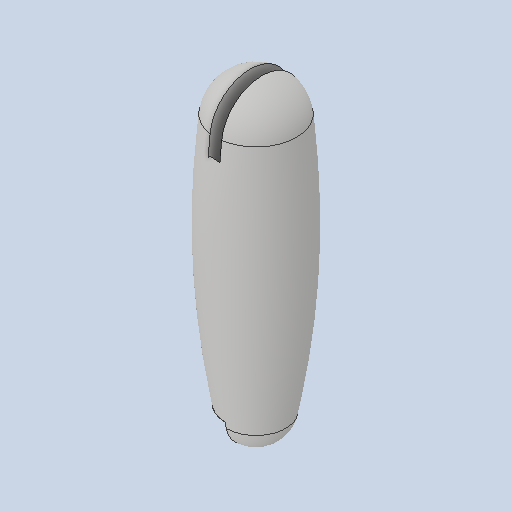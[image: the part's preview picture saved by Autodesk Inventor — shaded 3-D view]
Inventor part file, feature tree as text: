
AUTODESK INVENTOR PART (.ipt)
format: ipt  version: 2025 (Build 290162010, 162A)  size: 156,160 bytes
history: native  units: mm
features: sketch x4, revolve x2, extrude x2, other x1
ambient origin geometry x8: Origin, YZ Plane, XZ Plane, XY Plane, X Axis, Y Axis, Z Axis, Center Point
bodies: Body1 (feature_tree)
feature tree (9):
  other  "Твердое тело1"
  revolve  "Вращение1"
  extrude  "Выдавливание1"  Depth=140.0mm
  revolve  "Вращение2"
  extrude  "Выдавливание2"  Depth=104.0mm
  sketch  "Эскиз1"
  sketch  "Эскиз2"
  sketch  "Эскиз3"
  sketch  "Эскиз4"
